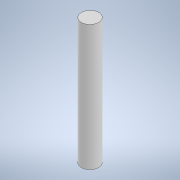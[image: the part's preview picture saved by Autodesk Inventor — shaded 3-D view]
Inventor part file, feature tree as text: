
AUTODESK INVENTOR PART (.ipt)
format: ipt  version: 2022 (Build 260153000, 153)  size: 90,624 bytes
history: native  units: mm
features: other x1, extrude x1, sketch x1
ambient origin geometry x8: Origin, YZ Plane, XZ Plane, XY Plane, X Axis, Y Axis, Z Axis, Center Point
bodies: Body1 (feature_tree)
feature tree (3):
  other  "ソリッド1"
  extrude  "押し出し1"  Depth=4.0mm
  sketch  "スケッチ1"
